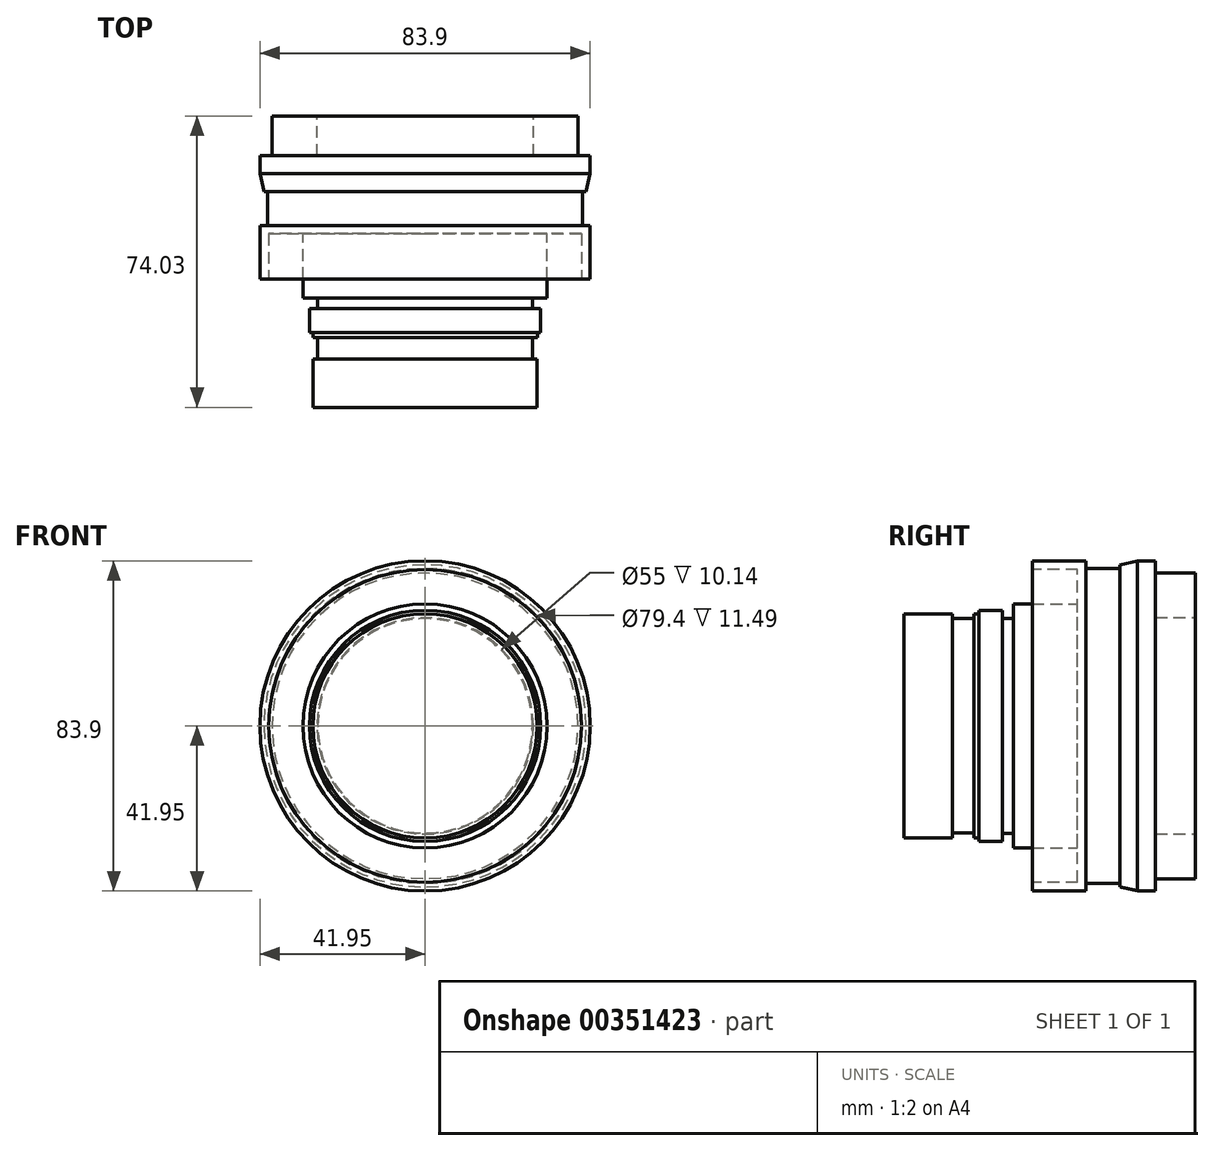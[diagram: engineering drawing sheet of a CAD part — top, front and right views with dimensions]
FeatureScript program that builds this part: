
annotation { "Feature Type Name" : "Feature", "Feature Type Description" : "" }
export const myFeature = defineFeature(function(context is Context, id is Id, definition is map)
    precondition{}
    {
        {
            var Q0;
            Q0=qCreatedBy(makeId("Front.planeOp"),FACE);
            var sketch = newSketch(context, id + "F0", { "sketchPlane" : qUnion([Q0])});
            skCircle(sketch, "E0", {"center": v(0, 0) * mm, "radius": 38.84 * mm});
            skCircle(sketch, "E1", {"center": v(0, 0) * mm, "radius": 27.5 * mm});
            skSolve(sketch);
        }
        {
            var Q0;
            Q0=qSketchRegion(id+"F0",true);
            extrude(context, id + "F1", {"entities" : qUnion([Q0]), "depth" : 10.14 * mm});
        }
        {
            var Q0;
            Q0=makeQuery(id+"F1.opExtrude","CAP_FACE",FACE,{"disambiguationData":[OSD([sQuery(id+"F0.wireOp",EDGE,"E0"),sQuery(id+"F0.wireOp",EDGE,"E1")])],"isStart":false});
            var sketch = newSketch(context, id + "F2", { "sketchPlane" : qUnion([Q0])});
            skCircle(sketch, "E2", {"center": v(0, 0) * mm, "radius": 41.88 * mm});
            skSolve(sketch);
        }
        {
            var Q0;
            Q0=qSketchRegion(id+"F2",true);
            extrude(context, id + "F3", {"entities" : qUnion([Q0]), "operationType" : NewBodyOperationType.ADD, "depth" : 4.57 * mm});
        }
        {
            var Q0;
            Q0=makeQuery(id+"F3.opExtrude","CAP_FACE",FACE,{"disambiguationData":[OSD([sQuery(id+"F2.wireOp",EDGE,"E2")])],"isStart":false});
            var sketch = newSketch(context, id + "F4", { "sketchPlane" : qUnion([Q0])});
            skCircle(sketch, "E3", {"center": v(0, 0) * mm, "radius": 41.88 * mm});
            skSolve(sketch);
        }
        {
            var Q0;
            Q0=makeQuery(id+"F4.imprint","IMPRINT",FACE,{"disambiguationData":[TD([[makeQuery(id+"F4.imprint","IMPRINT",EDGE,{"derivedFrom":sQuery(id+"F4.wireOp",EDGE,"E3")}),1.0]])]});
            cPlane(context, id + "F5", {"entities" : qUnion([Q0]), "cplaneType" : CPlaneType.OFFSET, "offset" : 4.5 * mm, "width" : 150 * mm, "height" : 150 * mm});
        }
        {
            var Q0;
            Q0=qCreatedBy(id+"F5.planeOp",FACE);
            var sketch = newSketch(context, id + "F6", { "sketchPlane" : qUnion([Q0])});
            skCircle(sketch, "E4", {"center": v(0, 0) * mm, "radius": 40.92 * mm});
            skSolve(sketch);
        }
        {
            var Q1;
            Q1=qSketchRegion(id+"F4",true);
            var Q2;
            Q2=qSketchRegion(id+"F6",true);
            loft(context, id + "F7", {"operationType" : NewBodyOperationType.ADD, "sheetProfilesArray" : [{ "sheetProfileEntities" : qUnion([Q1]) }, { "sheetProfileEntities" : qUnion([Q2]) }]});
        }
        {
            var Q0;
            Q0=makeQuery(id+"F7.opLoft","CAP_FACE",FACE,{"disambiguationData":[OSD([makeQuery(id+"F6.imprint","IMPRINT",FACE,{"disambiguationData":[TD([[makeQuery(id+"F6.imprint","IMPRINT",EDGE,{"derivedFrom":sQuery(id+"F6.wireOp",EDGE,"E4")}),1.0]])]})])],"isStart":true});
            var sketch = newSketch(context, id + "F8", { "sketchPlane" : qUnion([Q0])});
            skCircle(sketch, "E5", {"center": v(0, 0) * mm, "radius": 40 * mm});
            skSolve(sketch);
        }
        {
            var Q0;
            Q0=qSketchRegion(id+"F8",true);
            extrude(context, id + "F9", {"entities" : qUnion([Q0]), "operationType" : NewBodyOperationType.ADD, "depth" : 8.65 * mm});
        }
        {
            var Q0;
            Q0=makeQuery(id+"F9.opExtrude","CAP_FACE",FACE,{"disambiguationData":[OSD([sQuery(id+"F8.wireOp",EDGE,"E5")])],"isStart":false});
            var sketch = newSketch(context, id + "F10", { "sketchPlane" : qUnion([Q0])});
            skCircle(sketch, "E6", {"center": v(0, 0) * mm, "radius": 41.95 * mm});
            skSolve(sketch);
        }
        {
            var Q0;
            Q0=qSketchRegion(id+"F10",true);
            extrude(context, id + "F11", {"entities" : qUnion([Q0]), "operationType" : NewBodyOperationType.ADD, "depth" : 13.57 * mm});
        }
        {
            var Q0;
            Q0=makeQuery(id+"F11.opExtrude","CAP_FACE",FACE,{"disambiguationData":[OSD([sQuery(id+"F10.wireOp",EDGE,"E6")])],"isStart":false});
            var sketch = newSketch(context, id + "F12", { "sketchPlane" : qUnion([Q0])});
            skCircle(sketch, "E7", {"center": v(0, 0) * mm, "radius": 39.7 * mm});
            skSolve(sketch);
        }
        {
            var Q0;
            Q0=qSketchRegion(id+"F12",true);
            extrude(context, id + "F13", {"entities" : qUnion([Q0]), "operationType" : NewBodyOperationType.REMOVE, "oppositeDirection" : true, "depth" : 11.5 * mm});
        }
        {
            var Q0;
            Q0=makeQuery(id+"F13.boolean.opBoolean","COPY",FACE,{"derivedFrom":makeQuery(id+"F13.opExtrude","CAP_FACE",FACE,{"disambiguationData":[OSD([sQuery(id+"F12.wireOp",EDGE,"E7")])],"isStart":false})});
            var sketch = newSketch(context, id + "F14", { "sketchPlane" : qUnion([Q0])});
            skCircle(sketch, "E8", {"center": v(0, 0) * mm, "radius": 31 * mm});
            skSolve(sketch);
        }
        {
            var Q0;
            Q0=qSketchRegion(id+"F14",true);
            extrude(context, id + "F15", {"entities" : qUnion([Q0]), "operationType" : NewBodyOperationType.ADD, "depth" : 16.29 * mm});
        }
        {
            var Q0;
            Q0=makeQuery(id+"F15.opExtrude","CAP_FACE",FACE,{"disambiguationData":[OSD([sQuery(id+"F14.wireOp",EDGE,"E8")])],"isStart":false});
            var sketch = newSketch(context, id + "F16", { "sketchPlane" : qUnion([Q0])});
            skCircle(sketch, "E9", {"center": v(0, 0) * mm, "radius": 27.3 * mm});
            skSolve(sketch);
        }
        {
            var Q0;
            Q0=qSketchRegion(id+"F16",true);
            extrude(context, id + "F17", {"entities" : qUnion([Q0]), "operationType" : NewBodyOperationType.ADD, "depth" : 2.75 * mm});
        }
        {
            var Q0;
            Q0=makeQuery(id+"F17.opExtrude","CAP_FACE",FACE,{"disambiguationData":[OSD([sQuery(id+"F16.wireOp",EDGE,"E9")])],"isStart":false});
            var sketch = newSketch(context, id + "F18", { "sketchPlane" : qUnion([Q0])});
            skCircle(sketch, "E10", {"center": v(0, 0) * mm, "radius": 29.38 * mm});
            skSolve(sketch);
        }
        {
            var Q0;
            Q0=qSketchRegion(id+"F18",true);
            extrude(context, id + "F19", {"entities" : qUnion([Q0]), "operationType" : NewBodyOperationType.ADD, "depth" : 6 * mm});
        }
        {
            var Q0;
            Q0=makeQuery(id+"F19.opExtrude","CAP_FACE",FACE,{"disambiguationData":[OSD([sQuery(id+"F18.wireOp",EDGE,"E10")])],"isStart":false});
            var sketch = newSketch(context, id + "F20", { "sketchPlane" : qUnion([Q0])});
            skCircle(sketch, "E11", {"center": v(0, 0) * mm, "radius": 28.5 * mm});
            skSolve(sketch);
        }
        {
            var Q0;
            Q0=qSketchRegion(id+"F20",true);
            extrude(context, id + "F21", {"entities" : qUnion([Q0]), "operationType" : NewBodyOperationType.ADD, "depth" : 1.3 * mm});
        }
        {
            var Q0;
            Q0=makeQuery(id+"F21.opExtrude","CAP_FACE",FACE,{"disambiguationData":[OSD([sQuery(id+"F20.wireOp",EDGE,"E11")])],"isStart":false});
            var sketch = newSketch(context, id + "F22", { "sketchPlane" : qUnion([Q0])});
            skCircle(sketch, "E12", {"center": v(0, 0) * mm, "radius": 27.25 * mm});
            skSolve(sketch);
        }
        {
            var Q0;
            Q0=qSketchRegion(id+"F22",true);
            extrude(context, id + "F23", {"entities" : qUnion([Q0]), "operationType" : NewBodyOperationType.ADD, "depth" : 5.5 * mm});
        }
        {
            var Q0;
            Q0=makeQuery(id+"F23.opExtrude","CAP_FACE",FACE,{"disambiguationData":[OSD([sQuery(id+"F22.wireOp",EDGE,"E12")])],"isStart":false});
            var sketch = newSketch(context, id + "F24", { "sketchPlane" : qUnion([Q0])});
            skCircle(sketch, "E13", {"center": v(0, 0) * mm, "radius": 28.48 * mm});
            skSolve(sketch);
        }
        {
            var Q0;
            Q0=qSketchRegion(id+"F24",true);
            extrude(context, id + "F25", {"entities" : qUnion([Q0]), "operationType" : NewBodyOperationType.ADD, "depth" : 12.25 * mm});
        }
    });
